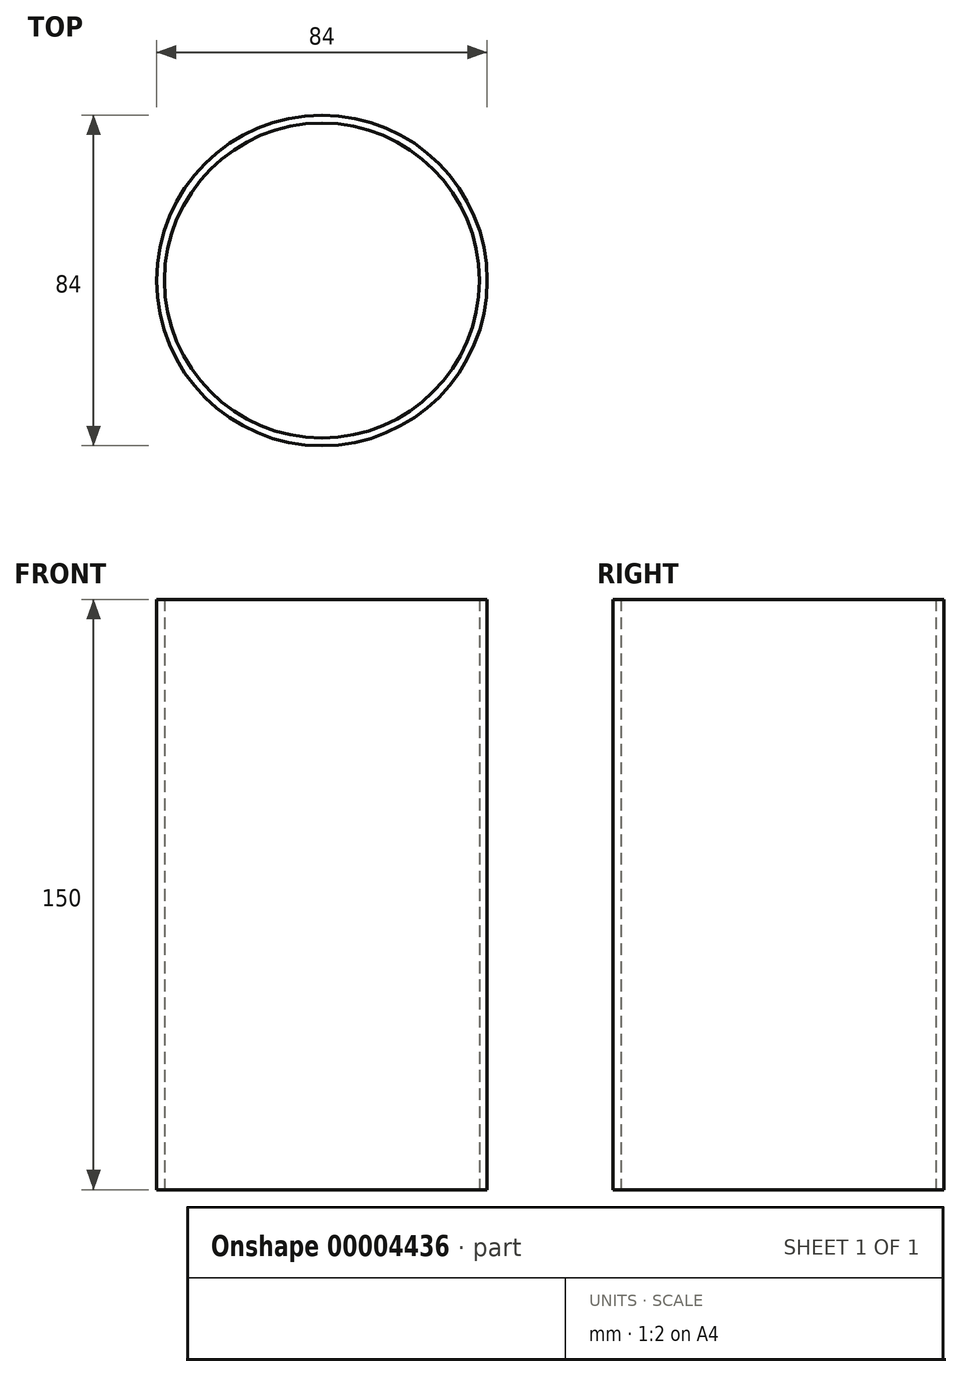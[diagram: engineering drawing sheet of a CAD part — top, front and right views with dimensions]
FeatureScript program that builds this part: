
annotation { "Feature Type Name" : "Feature", "Feature Type Description" : "" }
export const myFeature = defineFeature(function(context is Context, id is Id, definition is map)
    precondition{}
    {
        {
            var Q0;
            Q0=qCreatedBy(makeId("Top.planeOp"),FACE);
            var sketch = newSketch(context, id + "F0", { "sketchPlane" : qUnion([Q0])});
            skCircle(sketch, "E0", {"center": v(0, 0) * mm, "radius": 42 * mm});
            skCircle(sketch, "E1", {"center": v(0, 0) * mm, "radius": 40 * mm});
            skSolve(sketch);
        }
        {
            var Q0;
            Q0=makeQuery(id+"F0.imprint","IMPRINT",FACE,{"disambiguationData":[TD([[makeQuery(id+"F0.imprint","IMPRINT",EDGE,{"derivedFrom":sQuery(id+"F0.wireOp",EDGE,"E0")}),1.0]])]});
            extrude(context, id + "F1", {"entities" : qUnion([Q0]), "depth" : (140 + 10) * mm});
        }
    });
